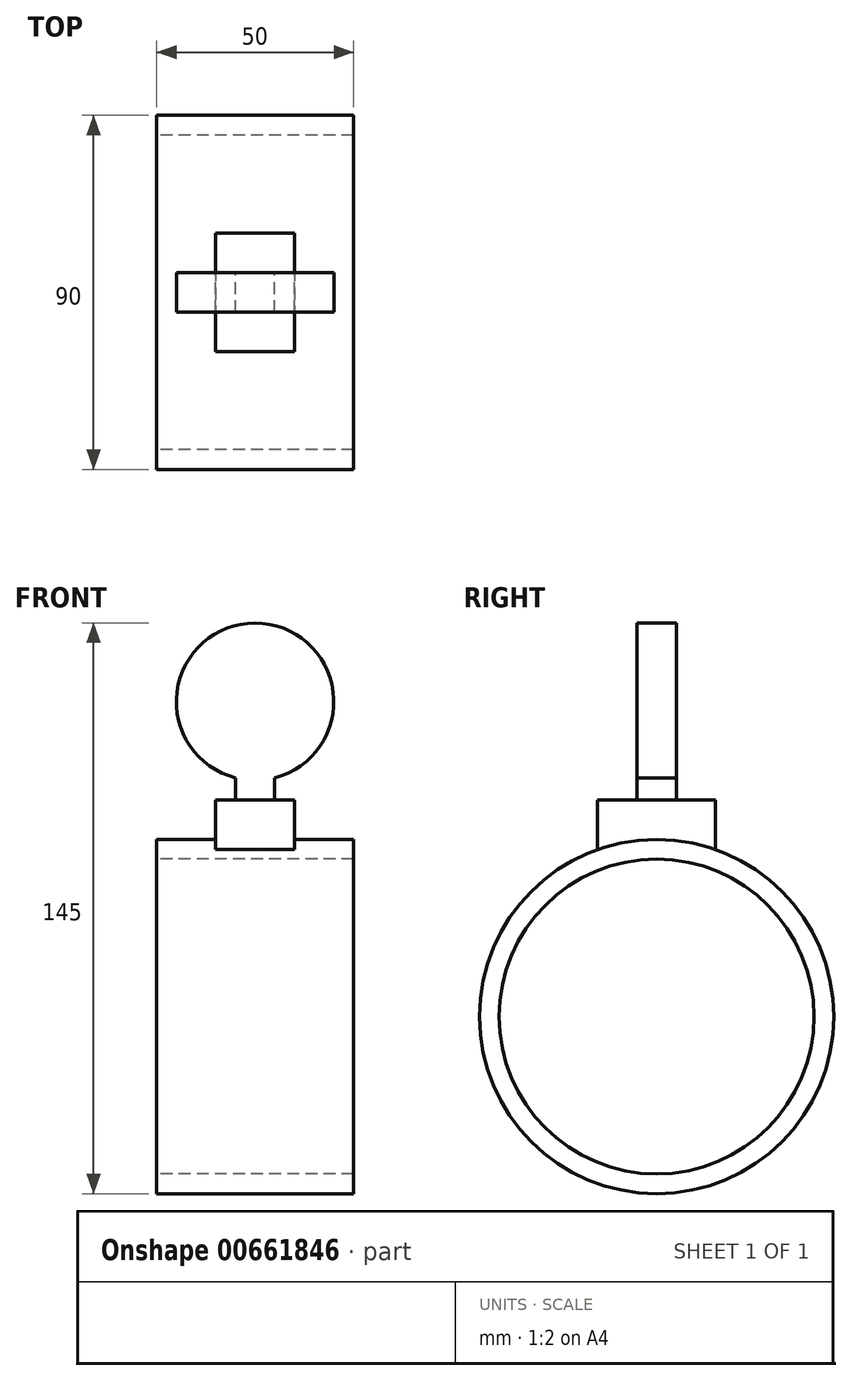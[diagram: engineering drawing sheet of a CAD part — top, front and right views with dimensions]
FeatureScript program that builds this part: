
annotation { "Feature Type Name" : "Feature", "Feature Type Description" : "" }
export const myFeature = defineFeature(function(context is Context, id is Id, definition is map)
    precondition{}
    {
        {
            var Q0;
            Q0=qCreatedBy(makeId("Right.planeOp"),FACE);
            var sketch = newSketch(context, id + "F0", { "sketchPlane" : qUnion([Q0])});
            skCircle(sketch, "E0", {"center": v(0, 0) * mm, "radius": 45 * mm});
            skCircle(sketch, "E1.0", {"center": v(0, 0) * mm, "radius": 40 * mm});
            skLineSegment(sketch, "E2", {"start": v(-15, 42.43) * mm, "end": v(-15, 55) * mm});
            skLineSegment(sketch, "E3", {"start": v(-15, 55) * mm, "end": v(15, 55) * mm});
            skLineSegment(sketch, "E4", {"start": v(15, 55) * mm, "end": v(15, 42.43) * mm});
            skSolve(sketch);
        }
        {
            var Q0;
            Q0=makeQuery(id+"F0.imprint","IMPRINT",FACE,{"disambiguationData":[TD([[makeQuery(id+"F0.imprint","IMPRINT",EDGE,{"derivedFrom":sQuery(id+"F0.wireOp",EDGE,"E1.0")}),-1.0]])]});
            extrude(context, id + "F1", {"entities" : qUnion([Q0]), "endBound" : BoundingType.SYMMETRIC, "depth" : 50 * mm, "offsetDistance" : 25 * mm});
        }
        {
            var Q0;
            {var subQ0=sQuery(id+"F0.wireOp",EDGE,"E2");Q0=makeQuery(id+"F0.imprint","IMPRINT",FACE,{"disambiguationData":[TD([[makeQuery(id+"F0.imprint","IMPRINT",EDGE,{"derivedFrom":subQ0}),-1.0]])]});}
            extrude(context, id + "F2", {"entities" : qUnion([Q0]), "operationType" : NewBodyOperationType.ADD, "endBound" : BoundingType.SYMMETRIC, "depth" : 20 * mm, "offsetDistance" : 25 * mm});
        }
        {
            var Q0;
            Q0=qCreatedBy(makeId("Front.planeOp"),FACE);
            var sketch = newSketch(context, id + "F3", { "sketchPlane" : qUnion([Q0])});
            skLineSegment(sketch, "E5.0", {"start": v(10, 55) * mm, "end": v(-10, 55) * mm});
            skCircle(sketch, "E6", {"center": v(0, 80) * mm, "radius": 20 * mm});
            skLineSegment(sketch, "E7", {"start": v(-5, 60.64) * mm, "end": v(-5, 55) * mm});
            skLineSegment(sketch, "E8", {"start": v(5, 60.64) * mm, "end": v(5, 55) * mm});
            skSolve(sketch);
        }
        {
            var Q0;
            {var subQ0=sQuery(id+"F3.wireOp",EDGE,"E6");var subQ1=makeQuery(id+"F3.imprint","INTERSECT",VERTEX,{"derivedFrom":[subQ0,sQuery(id+"F3.wireOp",EDGE,"E7")]});Q0=makeQuery(id+"F3.imprint","IMPRINT",FACE,{"disambiguationData":[TD([[makeQuery(id+"F3.imprint","IMPRINT",EDGE,{"disambiguationData":[TD([[subQ1,-1.0]])],"derivedFrom":subQ0}),1.0]])]});}
            var Q1;
            {var subQ0=sQuery(id+"F3.wireOp",EDGE,"E7");Q1=makeQuery(id+"F3.imprint","IMPRINT",FACE,{"disambiguationData":[TD([[makeQuery(id+"F3.imprint","IMPRINT",EDGE,{"derivedFrom":subQ0}),1.0]])]});}
            extrude(context, id + "F4", {"entities" : qUnion([Q0, Q1]), "operationType" : NewBodyOperationType.ADD, "endBound" : BoundingType.SYMMETRIC, "depth" : 10 * mm, "offsetDistance" : 25 * mm});
        }
    });
